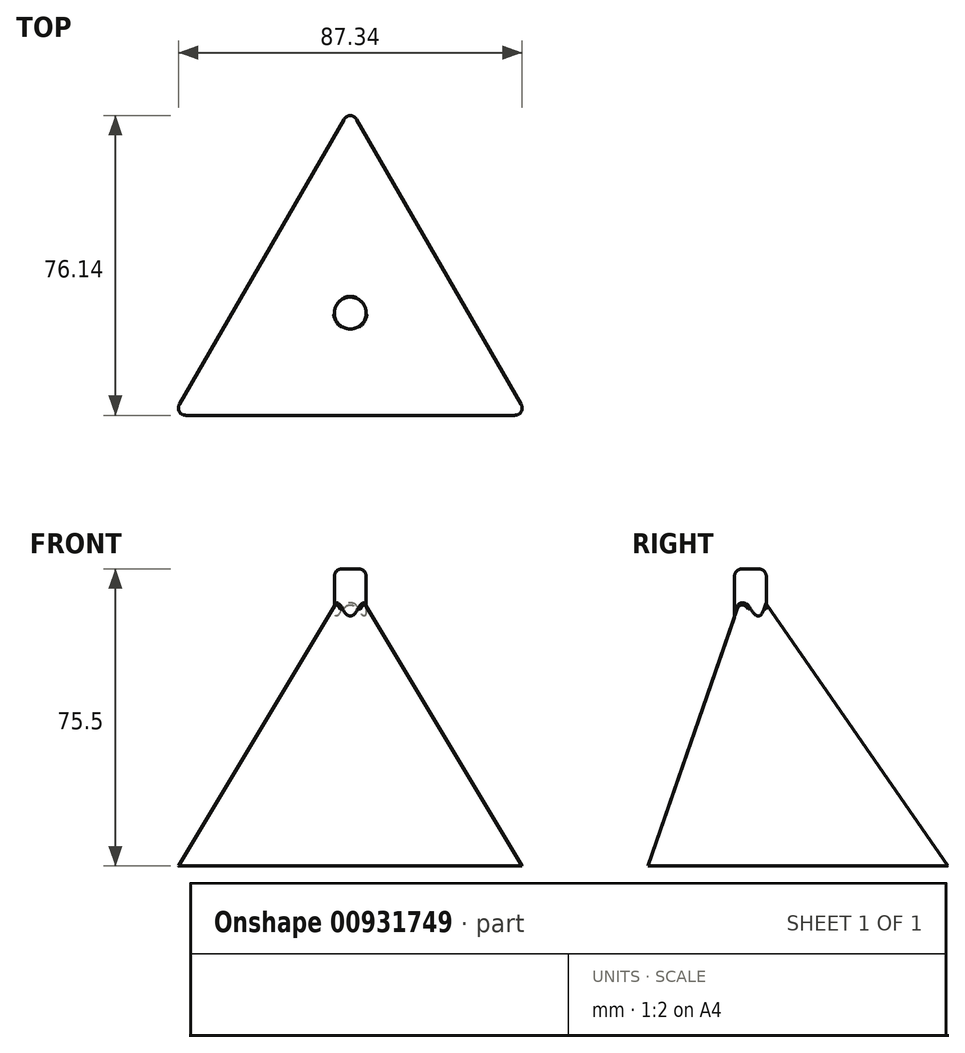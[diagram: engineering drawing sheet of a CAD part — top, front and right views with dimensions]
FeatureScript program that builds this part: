
annotation { "Feature Type Name" : "Feature", "Feature Type Description" : "" }
export const myFeature = defineFeature(function(context is Context, id is Id, definition is map)
    precondition{}
    {
        {
            var Q0;
            Q0=qCreatedBy(makeId("Top.planeOp"),FACE);
            var sketch = newSketch(context, id + "F0", { "sketchPlane" : qUnion([Q0])});
            skCircle(sketch, "E0.cCircle", {"center": v(0, 0) * mm, "radius": 25.98 * mm, "construction": true});
            skLineSegment(sketch, "E0.0", {"start": v(45, -25.98) * mm, "end": v(-45, -25.98) * mm});
            skLineSegment(sketch, "E0.1", {"start": v(-45, -25.98) * mm, "end": v(0, 51.96) * mm});
            skLineSegment(sketch, "E0.2", {"start": v(0, 51.96) * mm, "end": v(45, -25.98) * mm});
            skPoint(sketch, "E0.0.midPoint", {"position": v(0, -25.98) * mm});
            skSolve(sketch);
        }
        {
            var Q0;
            Q0=makeQuery(id+"F0.imprint","IMPRINT",FACE,{"disambiguationData":[TD([[makeQuery(id+"F0.imprint","IMPRINT",EDGE,{"derivedFrom":sQuery(id+"F0.wireOp",EDGE,"E0.0")}),-1.0]])]});
            cPlane(context, id + "F1", {"entities" : qUnion([Q0]), "cplaneType" : CPlaneType.OFFSET, "offset" : 75 * mm, "width" : 150 * mm, "height" : 150 * mm});
        }
        {
            var Q0;
            Q0=qCreatedBy(id+"F1.planeOp",FACE);
            var sketch = newSketch(context, id + "F2", { "sketchPlane" : qUnion([Q0])});
            skPoint(sketch, "E1", {"position": v(0, 0) * mm});
            skSolve(sketch);
        }
        {
            var Q0;
            Q0=makeQuery(id+"F0.imprint","IMPRINT",FACE,{"disambiguationData":[TD([[makeQuery(id+"F0.imprint","IMPRINT",EDGE,{"derivedFrom":sQuery(id+"F0.wireOp",EDGE,"E0.0")}),-1.0]])]});
            var Q1;
            Q1=sQuery(id+"F2.wireOp",VERTEX,"E1");
            loft(context, id + "F3", {"sheetProfilesArray" : [{ "sheetProfileEntities" : qUnion([Q0]) }, { "sheetProfileEntities" : qUnion([Q1]) }]});
        }
        {
            var Q0;
            Q0=qCreatedBy(id+"F1.planeOp",FACE);
            var sketch = newSketch(context, id + "F4", { "sketchPlane" : qUnion([Q0])});
            skCircle(sketch, "E2", {"center": v(0, 0) * mm, "radius": 4.05 * mm});
            skSolve(sketch);
        }
        {
            var Q0;
            Q0 = qSketchRegion(id + "F4", true);
            extrude(context, id + "F5", {"entities" : qUnion([Q0]), "operationType" : NewBodyOperationType.ADD, "depth" : 0.5 * mm, "offsetDistance" : 25 * mm, "hasSecondDirection" : true, "secondDirectionOppositeDirection" : true, "secondDirectionDepth" : 25 * mm});
        }
        {
            var Q0;
            Q0=makeQuery(id+"F3.opLoft","SWEPT_EDGE",EDGE,{"disambiguationData":[OSD([sQuery(id+"F0.wireOp",EDGE,"E0.1"),sQuery(id+"F0.wireOp",EDGE,"E0.2"),sQuery(id+"F2.wireOp",VERTEX,"E1")])]});
            var Q1;
            Q1=makeQuery(id+"F3.opLoft","SWEPT_EDGE",EDGE,{"disambiguationData":[OSD([sQuery(id+"F0.wireOp",EDGE,"E0.0"),sQuery(id+"F0.wireOp",EDGE,"E0.1"),sQuery(id+"F2.wireOp",VERTEX,"E1")])]});
            var Q2;
            Q2=makeQuery(id+"F3.opLoft","SWEPT_EDGE",EDGE,{"disambiguationData":[OSD([sQuery(id+"F0.wireOp",EDGE,"E0.0"),sQuery(id+"F0.wireOp",EDGE,"E0.2"),sQuery(id+"F2.wireOp",VERTEX,"E1")])]});
            fillet(context, id + "F6", {"entities" : qUnion([Q0, Q1, Q2]), "radius" : 2 * mm, "tangentPropagation" : true, "allowEdgeOverflow" : false});
        }
        {
            var Q0;
            Q0=makeQuery(id+"F5.opExtrude","CAP_EDGE",EDGE,{"disambiguationData":[OSD([sQuery(id+"F4.wireOp",EDGE,"E2")])],"isStart":false});
            fillet(context, id + "F7", {"entities" : qUnion([Q0]), "radius" : 2 * mm, "tangentPropagation" : true, "allowEdgeOverflow" : false});
        }
        {
            var Q0;
            {var subQ0=sQuery(id+"F0.wireOp",EDGE,"E0.0");var subQ1=sQuery(id+"F0.wireOp",EDGE,"E0.1");var subQ2=sQuery(id+"F0.wireOp",EDGE,"E0.2");Q0=makeQuery(id+"F5.boolean.opBoolean","INTERSECT",EDGE,{"derivedFrom":[makeQuery(id+"F3.opLoft","SWEPT_FACE",FACE,{"disambiguationData":[OSD([subQ0,subQ1,subQ2]),TDD([makeQuery(id+"F0.imprint","INTERSECT",VERTEX,{"derivedFrom":[subQ0,subQ2]}),makeQuery(id+"F0.imprint","INTERSECT",VERTEX,{"derivedFrom":[subQ0,subQ1]}),makeQuery(id+"F0.imprint","IMPRINT",EDGE,{"derivedFrom":subQ0})])]}),makeQuery(id+"F5.opExtrude","SWEPT_FACE",FACE,{"disambiguationData":[OSD([sQuery(id+"F4.wireOp",EDGE,"E2")])]})]});}
            var Q1;
            Q1=makeQuery(id+"F6.opFillet","BLEND_EDGE",EDGE,{"blendedFrom":[makeQuery(id+"F3.opLoft","SWEPT_EDGE",EDGE,{"disambiguationData":[OSD([sQuery(id+"F0.wireOp",EDGE,"E0.0"),sQuery(id+"F0.wireOp",EDGE,"E0.2"),sQuery(id+"F2.wireOp",VERTEX,"E1")])]}),makeQuery(id+"F5.opExtrude","SWEPT_FACE",FACE,{"disambiguationData":[OSD([sQuery(id+"F4.wireOp",EDGE,"E2")])]})],"blendedInto":[makeQuery(id+"F5.opExtrude","SWEPT_FACE",FACE,{"disambiguationData":[OSD([sQuery(id+"F4.wireOp",EDGE,"E2")])]})]});
            var Q2;
            {var subQ0=sQuery(id+"F0.wireOp",EDGE,"E0.2");var subQ1=sQuery(id+"F0.wireOp",EDGE,"E0.1");var subQ2=sQuery(id+"F0.wireOp",EDGE,"E0.0");Q2=makeQuery(id+"F5.boolean.opBoolean","INTERSECT",EDGE,{"derivedFrom":[makeQuery(id+"F3.opLoft","SWEPT_FACE",FACE,{"disambiguationData":[OSD([subQ2,subQ1,subQ0]),TDD([makeQuery(id+"F0.imprint","INTERSECT",VERTEX,{"derivedFrom":[subQ2,subQ0]}),makeQuery(id+"F0.imprint","INTERSECT",VERTEX,{"derivedFrom":[subQ1,subQ0]}),makeQuery(id+"F0.imprint","IMPRINT",EDGE,{"derivedFrom":subQ0})])]}),makeQuery(id+"F5.opExtrude","SWEPT_FACE",FACE,{"disambiguationData":[OSD([sQuery(id+"F4.wireOp",EDGE,"E2")])]})]});}
            var Q3;
            Q3=makeQuery(id+"F6.opFillet","BLEND_EDGE",EDGE,{"blendedFrom":[makeQuery(id+"F3.opLoft","SWEPT_EDGE",EDGE,{"disambiguationData":[OSD([sQuery(id+"F0.wireOp",EDGE,"E0.0"),sQuery(id+"F0.wireOp",EDGE,"E0.1"),sQuery(id+"F2.wireOp",VERTEX,"E1")])]}),makeQuery(id+"F5.opExtrude","SWEPT_FACE",FACE,{"disambiguationData":[OSD([sQuery(id+"F4.wireOp",EDGE,"E2")])]})],"blendedInto":[makeQuery(id+"F5.opExtrude","SWEPT_FACE",FACE,{"disambiguationData":[OSD([sQuery(id+"F4.wireOp",EDGE,"E2")])]})]});
            var Q4;
            {var subQ0=sQuery(id+"F0.wireOp",EDGE,"E0.1");var subQ1=sQuery(id+"F0.wireOp",EDGE,"E0.2");var subQ2=sQuery(id+"F0.wireOp",EDGE,"E0.0");Q4=makeQuery(id+"F5.boolean.opBoolean","INTERSECT",EDGE,{"derivedFrom":[makeQuery(id+"F3.opLoft","SWEPT_FACE",FACE,{"disambiguationData":[OSD([subQ2,subQ0,subQ1]),TDD([makeQuery(id+"F0.imprint","INTERSECT",VERTEX,{"derivedFrom":[subQ2,subQ0]}),makeQuery(id+"F0.imprint","INTERSECT",VERTEX,{"derivedFrom":[subQ0,subQ1]}),makeQuery(id+"F0.imprint","IMPRINT",EDGE,{"derivedFrom":subQ0})])]}),makeQuery(id+"F5.opExtrude","SWEPT_FACE",FACE,{"disambiguationData":[OSD([sQuery(id+"F4.wireOp",EDGE,"E2")])]})]});}
            var Q5;
            Q5=makeQuery(id+"F6.opFillet","BLEND_EDGE",EDGE,{"blendedFrom":[makeQuery(id+"F3.opLoft","SWEPT_EDGE",EDGE,{"disambiguationData":[OSD([sQuery(id+"F0.wireOp",EDGE,"E0.1"),sQuery(id+"F0.wireOp",EDGE,"E0.2"),sQuery(id+"F2.wireOp",VERTEX,"E1")])]}),makeQuery(id+"F5.opExtrude","SWEPT_FACE",FACE,{"disambiguationData":[OSD([sQuery(id+"F4.wireOp",EDGE,"E2")])]})],"blendedInto":[makeQuery(id+"F5.opExtrude","SWEPT_FACE",FACE,{"disambiguationData":[OSD([sQuery(id+"F4.wireOp",EDGE,"E2")])]})]});
            fillet(context, id + "F8", {"entities" : qUnion([Q0, Q1, Q2, Q3, Q4, Q5]), "radius" : 1 * mm, "tangentPropagation" : true, "allowEdgeOverflow" : false});
        }
    });
